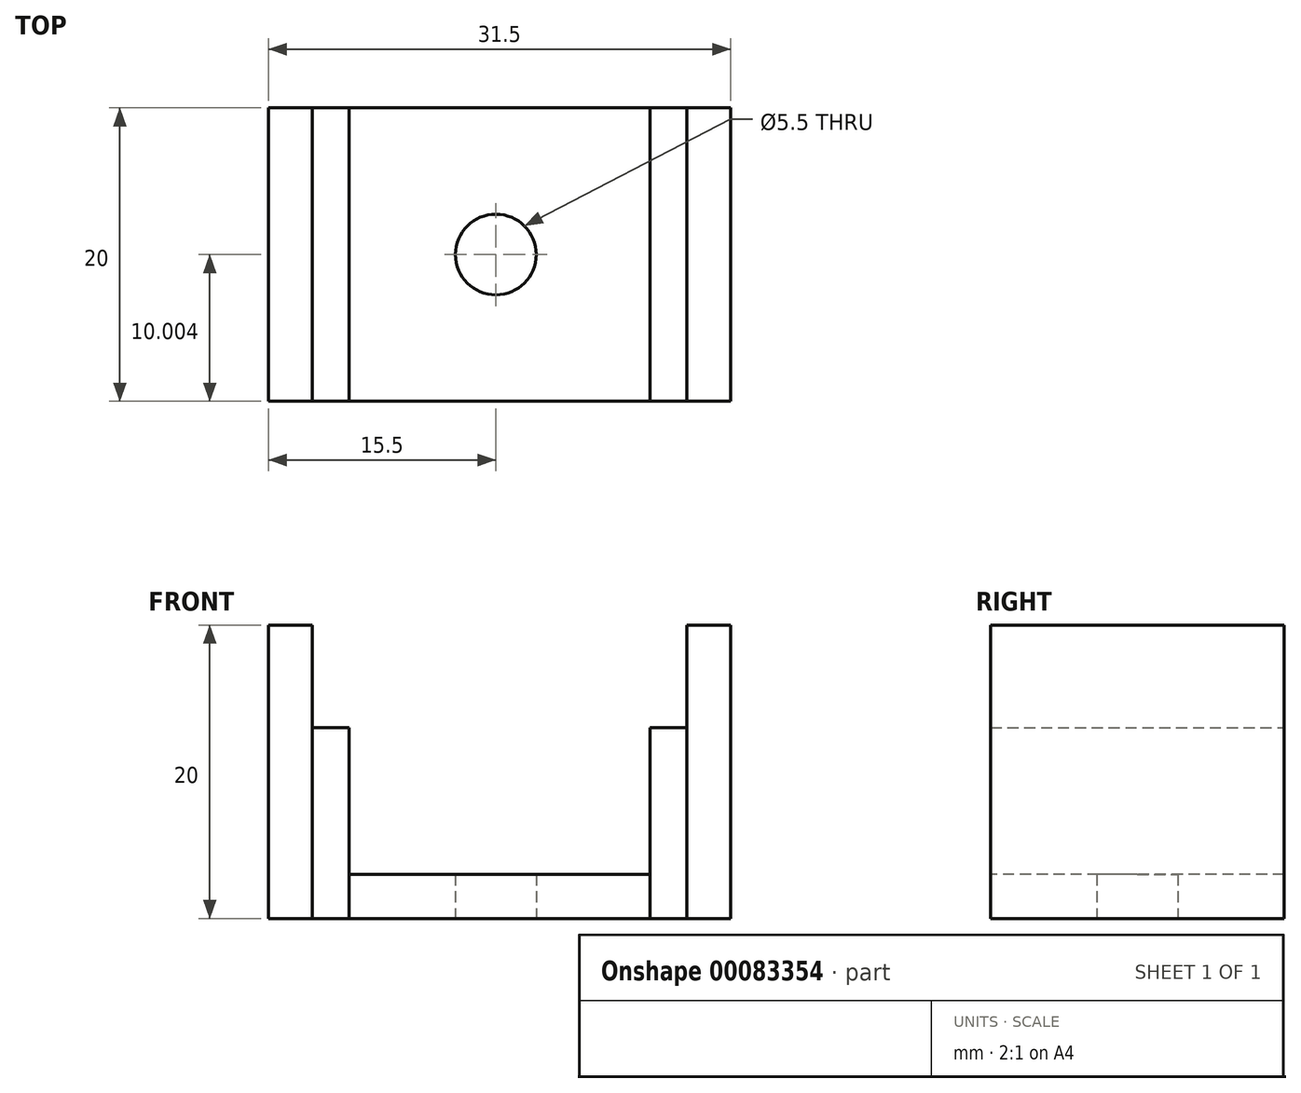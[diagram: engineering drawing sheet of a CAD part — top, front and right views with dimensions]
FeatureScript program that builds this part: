
annotation { "Feature Type Name" : "Feature", "Feature Type Description" : "" }
export const myFeature = defineFeature(function(context is Context, id is Id, definition is map)
    precondition{}
    {
        {
            var Q0;
            Q0=qCreatedBy(makeId("Top.planeOp"),FACE);
            var sketch = newSketch(context, id + "F0", { "sketchPlane" : qUnion([Q0])});
            skLineSegment(sketch, "E0.0", {"start": v(13, 8.45) * mm, "end": v(13, -11.55) * mm});
            skLineSegment(sketch, "E1.0", {"start": v(-12.5, -11.55) * mm, "end": v(-12.5, 8.45) * mm});
            skLineSegment(sketch, "E2", {"start": v(13, 8.45) * mm, "end": v(-12.5, 8.45) * mm});
            skLineSegment(sketch, "E3", {"start": v(13, -11.55) * mm, "end": v(-12.5, -11.55) * mm});
            skLineSegment(sketch, "E4.0", {"start": v(12.5, -1.55) * mm, "end": v(-12.5, -1.55) * mm, "construction": true});
            skPoint(sketch, "E5", {"position": v(0, -1.55) * mm});
            skLineSegment(sketch, "E6.0", {"start": v(-15.5, -11.55) * mm, "end": v(-15.5, 8.45) * mm});
            skLineSegment(sketch, "E7.0", {"start": v(16, 8.45) * mm, "end": v(16, -11.55) * mm});
            skLineSegment(sketch, "E8", {"start": v(16, 8.45) * mm, "end": v(13, 8.45) * mm});
            skLineSegment(sketch, "E9", {"start": v(-12.5, 8.45) * mm, "end": v(-15.5, 8.45) * mm});
            skLineSegment(sketch, "E10", {"start": v(-15.5, -11.55) * mm, "end": v(-12.5, -11.55) * mm});
            skLineSegment(sketch, "E11", {"start": v(16, -11.55) * mm, "end": v(13, -11.55) * mm});
            skLineSegment(sketch, "E12.0", {"start": v(-10, -56.55) * mm, "end": v(-10, 8.45) * mm});
            skLineSegment(sketch, "E13.0", {"start": v(10.5, 8.45) * mm, "end": v(10.5, -56.55) * mm});
            skSolve(sketch);
        }
        {
            var Q0;
            {var subQ0=sQuery(id+"F0.wireOp",EDGE,"E12.0");Q0=makeQuery(id+"F0.imprint","IMPRINT",FACE,{"disambiguationData":[TD([[makeQuery(id+"F0.imprint","IMPRINT",EDGE,{"derivedFrom":subQ0}),-1.0]])]});}
            extrude(context, id + "F1", {"entities" : qUnion([Q0]), "depth" : 3 * mm});
        }
        {
            var Q0;
            Q0=makeQuery(id+"F0.imprint","IMPRINT",FACE,{"disambiguationData":[TD([[makeQuery(id+"F0.imprint","IMPRINT",EDGE,{"derivedFrom":sQuery(id+"F0.wireOp",EDGE,"E0.0")}),1.0]])]});
            var Q1;
            Q1=makeQuery(id+"F0.imprint","IMPRINT",FACE,{"disambiguationData":[TD([[makeQuery(id+"F0.imprint","IMPRINT",EDGE,{"derivedFrom":sQuery(id+"F0.wireOp",EDGE,"E1.0")}),1.0]])]});
            extrude(context, id + "F2", {"entities" : qUnion([Q0, Q1]), "operationType" : NewBodyOperationType.ADD, "depth" : 20 * mm});
        }
        {
            var Q0;
            Q0=sQuery(id+"F0.wireOp",VERTEX,"E5");
            var Q1;
            Q1=sQuery(id+"F0.wireOp",VERTEX,"60a31dc9-fbec-48dd-b8cd-f3a7e48459a1");
            var Q2;
            Q2=makeQuery(id+"F1.opExtrude","SWEPT_BODY",BODY,{"disambiguationData":[OSD([sQuery(id+"F0.wireOp",EDGE,"E0.0"),sQuery(id+"F0.wireOp",EDGE,"E1.0"),sQuery(id+"F0.wireOp",EDGE,"E2"),sQuery(id+"F0.wireOp",EDGE,"E3")])]});
            hole(context, id + "F3", {"style" : HoleStyle.SIMPLE, "endStyle" : HoleEndStyle.THROUGH, "oppositeDirection" : true, "holeDiameter" : 5.5 * mm, "locations" : qUnion([Q0, Q1]), "scope" : qUnion([Q2]), "isTappedThrough" : true});
        }
        {
            var Q0;
            {var subQ0=sQuery(id+"F0.wireOp",EDGE,"E0.0");Q0=makeQuery(id+"F0.imprint","IMPRINT",FACE,{"disambiguationData":[TD([[makeQuery(id+"F0.imprint","IMPRINT",EDGE,{"derivedFrom":subQ0}),-1.0]])]});}
            var Q1;
            {var subQ0=sQuery(id+"F0.wireOp",EDGE,"E1.0");Q1=makeQuery(id+"F0.imprint","IMPRINT",FACE,{"disambiguationData":[TD([[makeQuery(id+"F0.imprint","IMPRINT",EDGE,{"derivedFrom":subQ0}),-1.0]])]});}
            extrude(context, id + "F4", {"entities" : qUnion([Q0, Q1]), "depth" : 13 * mm});
        }
    });
